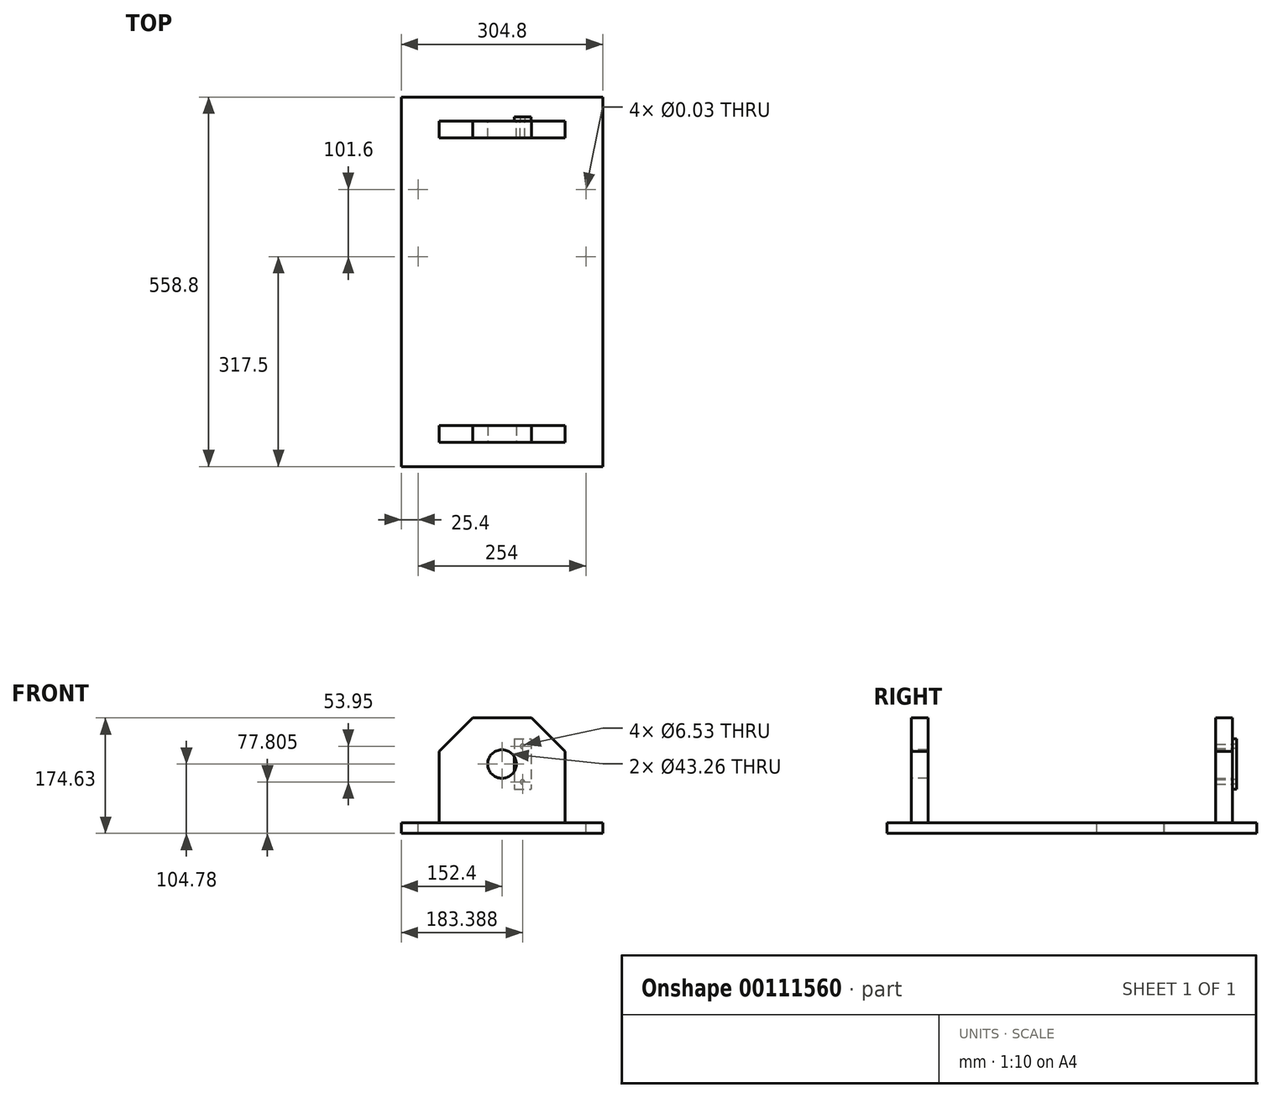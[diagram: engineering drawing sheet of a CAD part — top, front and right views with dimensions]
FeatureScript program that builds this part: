
annotation { "Feature Type Name" : "Feature", "Feature Type Description" : "" }
export const myFeature = defineFeature(function(context is Context, id is Id, definition is map)
    precondition{}
    {
        {
            var Q0;
            Q0=qCreatedBy(makeId("Top.planeOp"),FACE);
            var sketch = newSketch(context, id + "F0", { "sketchPlane" : qUnion([Q0])});
            skLineSegment(sketch, "E0.bottom", {"start": v(-152.4, 279.4) * mm, "end": v(152.4, 279.4) * mm});
            skLineSegment(sketch, "E0.top", {"start": v(-152.4, -279.4) * mm, "end": v(152.4, -279.4) * mm});
            skLineSegment(sketch, "E0.left", {"start": v(-152.4, 279.4) * mm, "end": v(-152.4, -279.4) * mm});
            skLineSegment(sketch, "E0.right", {"start": v(152.4, 279.4) * mm, "end": v(152.4, -279.4) * mm});
            skPoint(sketch, "E0.middle", {"position": v(0, 0) * mm});
            skSolve(sketch);
        }
        {
            var Q0;
            Q0 = qSketchRegion(id + "F0", true);
            extrude(context, id + "F1", {"entities" : qUnion([Q0]), "oppositeDirection" : true, "depth" : 15.88 * mm});
        }
        {
            var Q0;
            Q0=makeQuery(id+"F1.opExtrude","CAP_FACE",FACE,{"disambiguationData":[OSD([sQuery(id+"F0.wireOp",EDGE,"E0.bottom"),sQuery(id+"F0.wireOp",EDGE,"E0.top"),sQuery(id+"F0.wireOp",EDGE,"E0.left"),sQuery(id+"F0.wireOp",EDGE,"E0.right")])],"isStart":true});
            var sketch = newSketch(context, id + "F2", { "sketchPlane" : qUnion([Q0])});
            skLineSegment(sketch, "E1", {"start": v(0, 308.56) * mm, "end": v(0, -322.52) * mm, "construction": true});
            skPoint(sketch, "E1.endSnap0", {"position": v(0, -279.4) * mm});
            skLineSegment(sketch, "E2.0", {"start": v(-152.4, 279.4) * mm, "end": v(152.4, 279.4) * mm, "construction": true});
            skLineSegment(sketch, "E3.0", {"start": v(-152.4, 139.7) * mm, "end": v(152.4, 139.7) * mm, "construction": true});
            skLineSegment(sketch, "E4.0", {"start": v(-152.4, 38.1) * mm, "end": v(152.4, 38.1) * mm, "construction": true});
            skLineSegment(sketch, "E5.0", {"start": v(127, 308.56) * mm, "end": v(127, -322.52) * mm, "construction": true});
            skLineSegment(sketch, "E6.0", {"start": v(-127, 308.56) * mm, "end": v(-127, -322.52) * mm, "construction": true});
            skPoint(sketch, "E7", {"position": v(-127, 139.7) * mm});
            skPoint(sketch, "E8", {"position": v(-127, 38.1) * mm});
            skPoint(sketch, "E9", {"position": v(127, 38.1) * mm});
            skPoint(sketch, "E10", {"position": v(127, 139.7) * mm});
            skSolve(sketch);
        }
        {
            var Q0;
            Q0=sQuery(id+"F2.wireOp",VERTEX,"E7");
            var Q1;
            Q1=sQuery(id+"F2.wireOp",VERTEX,"E10");
            var Q2;
            Q2=sQuery(id+"F2.wireOp",VERTEX,"E9");
            var Q3;
            Q3=sQuery(id+"F2.wireOp",VERTEX,"E8");
            var Q4;
            Q4=makeQuery(id+"F1.opExtrude","SWEPT_BODY",BODY,{"disambiguationData":[OSD([sQuery(id+"F0.wireOp",EDGE,"E0.bottom"),sQuery(id+"F0.wireOp",EDGE,"E0.top"),sQuery(id+"F0.wireOp",EDGE,"E0.left"),sQuery(id+"F0.wireOp",EDGE,"E0.right")])]});
            hole(context, id + "F3", {"style" : HoleStyle.SIMPLE, "endStyle" : HoleEndStyle.THROUGH, "standardTappedOrClearance" : lookupTablePath({ "standard" : "ANSI", "size" : "7/8", "type" : "Drilled" }), "standardBlindInLast" : lookupTablePath({ "standard" : "ANSI", "size" : "7/8", "type" : "Drilled" }), "holeDiameter" : 7 / 203.2 * mm, "locations" : qUnion([Q0, Q1, Q2, Q3]), "scope" : qUnion([Q4]), "isTappedThrough" : true});
        }
        {
            var Q0;
            Q0=makeQuery(id+"F1.opExtrude","CAP_FACE",FACE,{"disambiguationData":[OSD([sQuery(id+"F0.wireOp",EDGE,"E0.bottom"),sQuery(id+"F0.wireOp",EDGE,"E0.top"),sQuery(id+"F0.wireOp",EDGE,"E0.left"),sQuery(id+"F0.wireOp",EDGE,"E0.right")])],"isStart":true});
            var sketch = newSketch(context, id + "F4", { "sketchPlane" : qUnion([Q0])});
            skLineSegment(sketch, "E11", {"start": v(-241.5, 0) * mm, "end": v(224.54, 0) * mm, "construction": true});
            skLineSegment(sketch, "E12.0", {"start": v(-241.5, 217.42) * mm, "end": v(224.54, 217.42) * mm, "construction": true});
            skLineSegment(sketch, "E13", {"start": v(0, 332.83) * mm, "end": v(0, -341.94) * mm, "construction": true});
            skPoint(sketch, "E13.startSnap0", {"position": v(0, 279.4) * mm});
            skLineSegment(sketch, "E14.0", {"start": v(-95.25, 332.83) * mm, "end": v(-95.25, -341.94) * mm, "construction": true});
            skLineSegment(sketch, "E15.bottom", {"start": v(-95.25, 217.42) * mm, "end": v(95.25, 217.42) * mm});
            skLineSegment(sketch, "E15.top", {"start": v(-95.25, 242.82) * mm, "end": v(95.25, 242.82) * mm});
            skLineSegment(sketch, "E15.left", {"start": v(-95.25, 217.42) * mm, "end": v(-95.25, 242.82) * mm});
            skLineSegment(sketch, "E15.right", {"start": v(95.25, 217.42) * mm, "end": v(95.25, 242.82) * mm});
            skSolve(sketch);
        }
        {
            var Q0;
            Q0 = qSketchRegion(id + "F4", true);
            extrude(context, id + "F5", {"entities" : qUnion([Q0]), "depth" : 158.75 * mm});
        }
        {
            var Q0;
            Q0=makeQuery(id+"F5.opExtrude","CAP_EDGE",EDGE,{"disambiguationData":[OSD([sQuery(id+"F4.wireOp",EDGE,"E15.right")])],"isStart":false});
            var Q1;
            Q1=makeQuery(id+"F5.opExtrude","CAP_EDGE",EDGE,{"disambiguationData":[OSD([sQuery(id+"F4.wireOp",EDGE,"E15.left")])],"isStart":false});
            chamfer(context, id + "F6", {"entities" : qUnion([Q0, Q1]), "width" : 50.8 * mm, "tangentPropagation" : true});
        }
        {
            var Q0;
            Q0=makeQuery(id+"F5.opExtrude","SWEPT_FACE",FACE,{"disambiguationData":[OSD([sQuery(id+"F4.wireOp",EDGE,"E15.top")])]});
            var sketch = newSketch(context, id + "F7", { "sketchPlane" : qUnion([Q0])});
            skLineSegment(sketch, "E16.0", {"start": v(44.45, 158.75) * mm, "end": v(-44.45, 158.75) * mm, "construction": true});
            skLineSegment(sketch, "E17", {"start": v(0, 158.75) * mm, "end": v(0, 28.34) * mm, "construction": true});
            skPoint(sketch, "E17.endSnap0", {"position": v(0, 158.75) * mm});
            skSolve(sketch);
        }
        {
            var Q0;
            {var subQ0=sQuery(id+"F4.wireOp",EDGE,"E15.top");Q0=makeQuery(id+"F7.imprint","IMPRINT",FACE,{"disambiguationData":[TD([[makeQuery(id+"F7.imprint","IMPRINT",EDGE,{"derivedFrom":makeQuery(id+"F5.opExtrude","CAP_EDGE",EDGE,{"disambiguationData":[OSD([subQ0])],"isStart":true})}),-1.0]])]});}
            var sketch = newSketch(context, id + "F8", { "sketchPlane" : qUnion([Q0])});
            skLineSegment(sketch, "E18.0", {"start": v(44.45, 158.75) * mm, "end": v(-44.45, 158.75) * mm, "construction": true});
            skLineSegment(sketch, "E19.0", {"start": v(44.45, 88.9) * mm, "end": v(-44.45, 88.9) * mm, "construction": true});
            skLineSegment(sketch, "E20.0", {"start": v(0, 158.75) * mm, "end": v(0, 28.34) * mm, "construction": true});
            skCircle(sketch, "E21", {"center": v(0, 88.9) * mm, "radius": 21.63 * mm});
            skSolve(sketch);
        }
        {
            var Q0;
            Q0 = qSketchRegion(id + "F8", true);
            extrude(context, id + "F9", {"entities" : qUnion([Q0]), "operationType" : NewBodyOperationType.REMOVE, "endBound" : BoundingType.THROUGH_ALL, "oppositeDirection" : true, "depth" : 25.4 * mm});
        }
        {
            var Q0;
            Q0=makeQuery(id+"F5.opExtrude","SWEPT_BODY",BODY,{"disambiguationData":[OSD([sQuery(id+"F4.wireOp",EDGE,"E15.bottom"),sQuery(id+"F4.wireOp",EDGE,"E15.top"),sQuery(id+"F4.wireOp",EDGE,"E15.left"),sQuery(id+"F4.wireOp",EDGE,"E15.right")])]});
            var Q1;
            Q1=qCreatedBy(makeId("Front.planeOp"),FACE);
            mirror(context, id + "F10", {"entities" : qUnion([Q0]), "mirrorPlane" : qUnion([Q1])});
        }
        {
            var Q0;
            {var subQ0=sQuery(id+"F4.wireOp",EDGE,"E15.top");Q0=makeQuery(id+"F7.imprint","IMPRINT",FACE,{"disambiguationData":[TD([[makeQuery(id+"F7.imprint","IMPRINT",EDGE,{"derivedFrom":makeQuery(id+"F5.opExtrude","CAP_EDGE",EDGE,{"disambiguationData":[OSD([subQ0])],"isStart":true})}),-1.0]])]});}
            var sketch = newSketch(context, id + "F11", { "sketchPlane" : qUnion([Q0])});
            skLineSegment(sketch, "E22.0", {"start": v(0, 158.75) * mm, "end": v(0, 28.34) * mm, "construction": true});
            skCircle(sketch, "E23.0", {"center": v(0, 88.9) * mm, "radius": 21.63 * mm, "construction": true});
            skLineSegment(sketch, "E24", {"start": v(-140.82, 88.9) * mm, "end": v(150.18, 88.9) * mm, "construction": true});
            skLineSegment(sketch, "E25.0", {"start": v(-30.99, 158.75) * mm, "end": v(-30.99, 28.34) * mm, "construction": true});
            skLineSegment(sketch, "E26.0", {"start": v(-140.82, 115.87) * mm, "end": v(150.18, 115.87) * mm, "construction": true});
            skLineSegment(sketch, "E27.MirrorCS", {"start": v(-140.82, 61.93) * mm, "end": v(150.18, 61.93) * mm, "construction": true});
            skPoint(sketch, "E28", {"position": v(-30.99, 115.87) * mm});
            skPoint(sketch, "E29", {"position": v(-30.99, 61.93) * mm});
            skSolve(sketch);
        }
        {
            var Q0;
            Q0=sQuery(id+"F11.wireOp",VERTEX,"E28");
            var Q1;
            Q1=sQuery(id+"F11.wireOp",VERTEX,"E29");
            var Q2;
            Q2=makeQuery(id+"F5.opExtrude","SWEPT_BODY",BODY,{"disambiguationData":[OSD([sQuery(id+"F4.wireOp",EDGE,"E15.bottom"),sQuery(id+"F4.wireOp",EDGE,"E15.top"),sQuery(id+"F4.wireOp",EDGE,"E15.left"),sQuery(id+"F4.wireOp",EDGE,"E15.right")])]});
            hole(context, id + "F12", {"style" : HoleStyle.SIMPLE, "endStyle" : HoleEndStyle.THROUGH, "standardTappedOrClearance" : lookupTablePath({ "standard" : "ANSI", "engagement" : "75%", "pitch" : "18 tpi", "size" : "5/16", "type" : "Tapped" }), "standardBlindInLast" : lookupTablePath({ "standard" : "ANSI", "engagement" : "75%", "pitch" : "18 tpi", "size" : "5/16", "type" : "Tapped" }), "holeDiameter" : 6.53 * mm, "locations" : qUnion([Q0, Q1]), "scope" : qUnion([Q2]), "isTappedThrough" : true, "majorDiameter" : 7.94 * mm, "showTappedDepth" : true});
        }
        {
            var Q0;
            {var subQ0=sQuery(id+"F4.wireOp",EDGE,"E15.top");Q0=makeQuery(id+"F7.imprint","IMPRINT",FACE,{"disambiguationData":[TD([[makeQuery(id+"F7.imprint","IMPRINT",EDGE,{"derivedFrom":makeQuery(id+"F5.opExtrude","CAP_EDGE",EDGE,{"disambiguationData":[OSD([subQ0])],"isStart":true})}),-1.0]])]});}
            var sketch = newSketch(context, id + "F13", { "sketchPlane" : qUnion([Q0])});
            skCircle(sketch, "E30.0", {"center": v(-30.99, 115.87) * mm, "radius": 3.26 * mm});
            skCircle(sketch, "E31.0", {"center": v(-30.99, 61.93) * mm, "radius": 3.26 * mm});
            skLineSegment(sketch, "E32", {"start": v(-30.99, 115.87) * mm, "end": v(-30.99, 61.93) * mm, "construction": true});
            skLineSegment(sketch, "E33.0", {"start": v(-18.29, 115.8) * mm, "end": v(-18.29, 61.85) * mm, "construction": true});
            skLineSegment(sketch, "E34.bottom", {"start": v(-18.29, 127) * mm, "end": v(-43.69, 127) * mm});
            skLineSegment(sketch, "E34.top", {"start": v(-18.29, 50.8) * mm, "end": v(-43.69, 50.8) * mm});
            skLineSegment(sketch, "E34.left", {"start": v(-18.29, 127) * mm, "end": v(-18.29, 50.8) * mm});
            skLineSegment(sketch, "E34.right", {"start": v(-43.69, 127) * mm, "end": v(-43.69, 50.8) * mm});
            skPoint(sketch, "E34.middle", {"position": v(-30.99, 88.9) * mm});
            skSolve(sketch);
        }
        {
            var Q0;
            Q0 = qSketchRegion(id + "F13", true);
            extrude(context, id + "F14", {"entities" : qUnion([Q0]), "depth" : 6.35 * mm});
        }
    });
